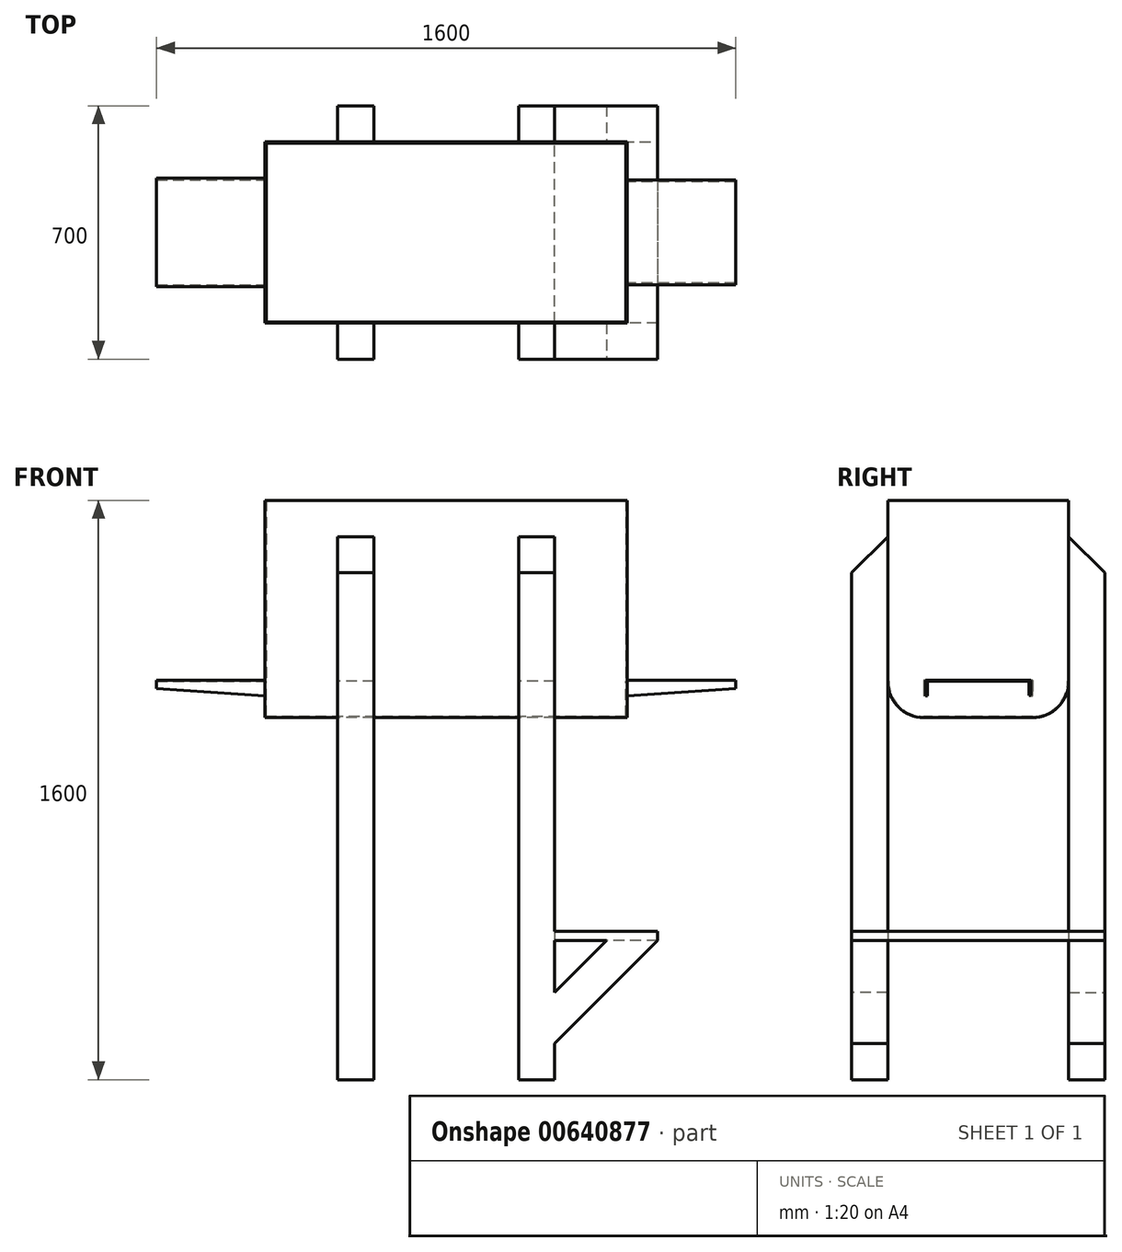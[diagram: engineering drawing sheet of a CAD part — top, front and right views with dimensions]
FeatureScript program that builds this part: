
annotation { "Feature Type Name" : "Feature", "Feature Type Description" : "" }
export const myFeature = defineFeature(function(context is Context, id is Id, definition is map)
    precondition{}
    {
        {
            var Q0;
            Q0=qCreatedBy(makeId("Right.planeOp"),FACE);
            var sketch = newSketch(context, id + "F0", { "sketchPlane" : qUnion([Q0])});
            skLineSegment(sketch, "E0", {"start": v(0, 632.77) * mm, "end": v(0, -64.43) * mm, "construction": true});
            skLineSegment(sketch, "E1", {"start": v(250, 600) * mm, "end": v(250, 100) * mm});
            skLineSegment(sketch, "E2", {"start": v(150, 0) * mm, "end": v(-150, 0) * mm});
            skLineSegment(sketch, "E3", {"start": v(-250, 100) * mm, "end": v(-250, 600) * mm});
            skPoint(sketch, "E4.visualSharp", {"position": v(250, 0) * mm});
            skArc(sketch, "E4.filletArc", {"start": v(150, 0) * mm, "mid": v(220.71, 29.29) * mm, "end": v(250, 100) * mm});
            skPoint(sketch, "E5.visualSharp", {"position": v(-250, 0) * mm});
            skArc(sketch, "E5.filletArc", {"start": v(-250, 100) * mm, "mid": v(-220.71, 29.29) * mm, "end": v(-150, 0) * mm});
            skLineSegment(sketch, "E6", {"start": v(250, 600) * mm, "end": v(-250, 600) * mm});
            skSolve(sketch);
        }
        {
            var Q0;
            Q0 = qSketchRegion(id + "F0", true);
            extrude(context, id + "F1", {"entities" : qUnion([Q0]), "depth" : 1000 * mm, "offsetDistance" : 25.4 * mm});
        }
        {
            var Q0;
            Q0=makeQuery(id+"F1.opExtrude","SWEPT_FACE",FACE,{"disambiguationData":[OSD([sQuery(id+"F0.wireOp",EDGE,"E6")])]});
            shell(context, id + "F2", {"entities" : qUnion([Q0]), "thickness" : 3 * mm});
        }
        {
            var Q0;
            Q0=makeQuery(id+"F1.opExtrude","CAP_FACE",FACE,{"disambiguationData":[OSD([sQuery(id+"F0.wireOp",EDGE,"E1"),sQuery(id+"F0.wireOp",EDGE,"E2"),sQuery(id+"F0.wireOp",EDGE,"E3"),sQuery(id+"F0.wireOp",EDGE,"E4.filletArc"),sQuery(id+"F0.wireOp",EDGE,"E5.filletArc"),sQuery(id+"F0.wireOp",EDGE,"E6")])],"isStart":true});
            var sketch = newSketch(context, id + "F3", { "sketchPlane" : qUnion([Q0])});
            skLineSegment(sketch, "E7.bottom", {"start": v(-150, 103) * mm, "end": v(150, 103) * mm});
            skLineSegment(sketch, "E7.top", {"start": v(-150, 100) * mm, "end": v(150, 100) * mm});
            skLineSegment(sketch, "E7.left", {"start": v(-150, 103) * mm, "end": v(-150, 100) * mm});
            skLineSegment(sketch, "E7.right", {"start": v(150, 103) * mm, "end": v(150, 100) * mm});
            skLineSegment(sketch, "E8", {"start": v(0, 372.57) * mm, "end": v(0, -47.43) * mm, "construction": true});
            skSolve(sketch);
        }
        {
            var Q0;
            Q0 = qSketchRegion(id + "F3", true);
            extrude(context, id + "F4", {"entities" : qUnion([Q0]), "operationType" : NewBodyOperationType.ADD, "depth" : 300 * mm, "offsetDistance" : 25.4 * mm});
        }
        {
            var Q0;
            Q0=makeQuery(id+"F4.opExtrude","SWEPT_FACE",FACE,{"disambiguationData":[OSD([sQuery(id+"F3.wireOp",EDGE,"E7.right")])]});
            var sketch = newSketch(context, id + "F5", { "sketchPlane" : qUnion([Q0])});
            skLineSegment(sketch, "E9", {"start": v(-300, 100) * mm, "end": v(-300, 80) * mm});
            skLineSegment(sketch, "E10", {"start": v(-300, 80) * mm, "end": v(0, 60) * mm});
            skLineSegment(sketch, "E11", {"start": v(0, 60) * mm, "end": v(0, 100) * mm});
            skLineSegment(sketch, "E12", {"start": v(-300, 100) * mm, "end": v(0, 100) * mm});
            skSolve(sketch);
        }
        {
            var Q0;
            Q0 = qSketchRegion(id + "F5", true);
            extrude(context, id + "F6", {"entities" : qUnion([Q0]), "operationType" : NewBodyOperationType.ADD, "oppositeDirection" : true, "depth" : 5 * mm, "offsetDistance" : 25.4 * mm});
        }
        {
            var Q0;
            Q0=makeQuery(id+"F4.opExtrude","SWEPT_FACE",FACE,{"disambiguationData":[OSD([sQuery(id+"F3.wireOp",EDGE,"E7.left")])]});
            var sketch = newSketch(context, id + "F7", { "sketchPlane" : qUnion([Q0])});
            skLineSegment(sketch, "E13", {"start": v(0, 100) * mm, "end": v(0, 60) * mm});
            skLineSegment(sketch, "E14", {"start": v(0, 60) * mm, "end": v(300, 80) * mm});
            skLineSegment(sketch, "E15", {"start": v(300, 80) * mm, "end": v(300, 100) * mm});
            skLineSegment(sketch, "E16", {"start": v(300, 100) * mm, "end": v(0, 100) * mm});
            skSolve(sketch);
        }
        {
            var Q0;
            Q0 = qSketchRegion(id + "F7", true);
            extrude(context, id + "F8", {"entities" : qUnion([Q0]), "operationType" : NewBodyOperationType.ADD, "oppositeDirection" : true, "depth" : 5 * mm, "offsetDistance" : 25.4 * mm});
        }
        {
            var Q0;
            Q0=makeQuery(id+"F1.opExtrude","SWEPT_FACE",FACE,{"disambiguationData":[OSD([sQuery(id+"F0.wireOp",EDGE,"E3")])]});
            var sketch = newSketch(context, id + "F9", { "sketchPlane" : qUnion([Q0])});
            skLineSegment(sketch, "E17", {"start": v(500, 727.75) * mm, "end": v(500, -77.26) * mm, "construction": true});
            skPoint(sketch, "E17.startSnap0", {"position": v(500, 600) * mm});
            skLineSegment(sketch, "E18.bottom", {"start": v(200, 500) * mm, "end": v(300, 500) * mm});
            skLineSegment(sketch, "E18.top", {"start": v(200, -1000) * mm, "end": v(300, -1000) * mm});
            skLineSegment(sketch, "E18.left", {"start": v(200, 500) * mm, "end": v(200, -1000) * mm});
            skLineSegment(sketch, "E18.right", {"start": v(300, 500) * mm, "end": v(300, -1000) * mm});
            skLineSegment(sketch, "E19.bottom", {"start": v(700, 500) * mm, "end": v(800, 500) * mm});
            skLineSegment(sketch, "E19.top", {"start": v(700, -1000) * mm, "end": v(800, -1000) * mm});
            skLineSegment(sketch, "E19.left", {"start": v(700, 500) * mm, "end": v(700, -1000) * mm});
            skLineSegment(sketch, "E19.right", {"start": v(800, 500) * mm, "end": v(800, -1000) * mm});
            skSolve(sketch);
        }
        {
            var Q0;
            Q0 = qSketchRegion(id + "F9", true);
            extrude(context, id + "F10", {"entities" : qUnion([Q0]), "operationType" : NewBodyOperationType.ADD, "depth" : 100 * mm, "offsetDistance" : 25.4 * mm});
        }
        {
            var Q0;
            Q0=makeQuery(id+"F10.opExtrude","SWEPT_FACE",FACE,{"disambiguationData":[OSD([sQuery(id+"F9.wireOp",EDGE,"E18.left")])]});
            var sketch = newSketch(context, id + "F11", { "sketchPlane" : qUnion([Q0])});
            skLineSegment(sketch, "E20", {"start": v(250, 500) * mm, "end": v(350, 400) * mm});
            skLineSegment(sketch, "E21", {"start": v(350, 400) * mm, "end": v(350, 500) * mm});
            skLineSegment(sketch, "E22", {"start": v(350, 500) * mm, "end": v(250, 500) * mm});
            skSolve(sketch);
        }
        {
            var Q0;
            Q0 = qSketchRegion(id + "F11", true);
            extrude(context, id + "F12", {"entities" : qUnion([Q0]), "operationType" : NewBodyOperationType.REMOVE, "endBound" : BoundingType.THROUGH_ALL, "oppositeDirection" : true, "depth" : 25.4 * mm, "offsetDistance" : 25.4 * mm});
        }
        {
            var Q0;
            Q0=makeQuery(id+"F1.opExtrude","SWEPT_FACE",FACE,{"disambiguationData":[OSD([sQuery(id+"F0.wireOp",EDGE,"E1")])]});
            var sketch = newSketch(context, id + "F13", { "sketchPlane" : qUnion([Q0])});
            skLineSegment(sketch, "E23", {"start": v(-500, 832.8) * mm, "end": v(-500, -264.24) * mm, "construction": true});
            skPoint(sketch, "E23.startSnap0", {"position": v(-500, 100) * mm});
            skLineSegment(sketch, "E24.bottom", {"start": v(-800, 500) * mm, "end": v(-700, 500) * mm});
            skLineSegment(sketch, "E24.top", {"start": v(-800, -1000) * mm, "end": v(-700, -1000) * mm});
            skLineSegment(sketch, "E24.left", {"start": v(-800, 500) * mm, "end": v(-800, -1000) * mm});
            skLineSegment(sketch, "E24.right", {"start": v(-700, 500) * mm, "end": v(-700, -1000) * mm});
            skLineSegment(sketch, "E25.bottom", {"start": v(-300, 500) * mm, "end": v(-200, 500) * mm});
            skLineSegment(sketch, "E25.top", {"start": v(-300, -1000) * mm, "end": v(-200, -1000) * mm});
            skLineSegment(sketch, "E25.left", {"start": v(-300, 500) * mm, "end": v(-300, -1000) * mm});
            skLineSegment(sketch, "E25.right", {"start": v(-200, 500) * mm, "end": v(-200, -1000) * mm});
            skSolve(sketch);
        }
        {
            var Q0;
            Q0 = qSketchRegion(id + "F13", true);
            extrude(context, id + "F14", {"entities" : qUnion([Q0]), "operationType" : NewBodyOperationType.ADD, "depth" : 100 * mm, "offsetDistance" : 25.4 * mm});
        }
        {
            var Q0;
            Q0=makeQuery(id+"F14.opExtrude","SWEPT_FACE",FACE,{"disambiguationData":[OSD([sQuery(id+"F13.wireOp",EDGE,"E24.left")])]});
            var sketch = newSketch(context, id + "F15", { "sketchPlane" : qUnion([Q0])});
            skLineSegment(sketch, "E26", {"start": v(250, 500) * mm, "end": v(350, 400) * mm});
            skLineSegment(sketch, "E27", {"start": v(350, 400) * mm, "end": v(350, 500) * mm});
            skLineSegment(sketch, "E28", {"start": v(350, 500) * mm, "end": v(250, 500) * mm});
            skSolve(sketch);
        }
        {
            var Q0;
            Q0 = qSketchRegion(id + "F15", true);
            extrude(context, id + "F16", {"entities" : qUnion([Q0]), "operationType" : NewBodyOperationType.REMOVE, "endBound" : BoundingType.THROUGH_ALL, "oppositeDirection" : true, "depth" : 25.4 * mm, "offsetDistance" : 25.4 * mm});
        }
        {
            var Q0;
            Q0=makeQuery(id+"F1.opExtrude","CAP_FACE",FACE,{"disambiguationData":[OSD([sQuery(id+"F0.wireOp",EDGE,"E1"),sQuery(id+"F0.wireOp",EDGE,"E2"),sQuery(id+"F0.wireOp",EDGE,"E3"),sQuery(id+"F0.wireOp",EDGE,"E4.filletArc"),sQuery(id+"F0.wireOp",EDGE,"E5.filletArc"),sQuery(id+"F0.wireOp",EDGE,"E6")])],"isStart":false});
            var sketch = newSketch(context, id + "F17", { "sketchPlane" : qUnion([Q0])});
            skLineSegment(sketch, "E29.bottom", {"start": v(-145, 103) * mm, "end": v(145, 103) * mm});
            skLineSegment(sketch, "E29.top", {"start": v(-145, 100) * mm, "end": v(145, 100) * mm});
            skLineSegment(sketch, "E29.left", {"start": v(-145, 103) * mm, "end": v(-145, 100) * mm});
            skLineSegment(sketch, "E29.right", {"start": v(145, 103) * mm, "end": v(145, 100) * mm});
            skLineSegment(sketch, "E30", {"start": v(0, 538.1) * mm, "end": v(0, -341.27) * mm, "construction": true});
            skSolve(sketch);
        }
        {
            var Q0;
            Q0 = qSketchRegion(id + "F17", true);
            extrude(context, id + "F18", {"entities" : qUnion([Q0]), "operationType" : NewBodyOperationType.ADD, "depth" : 300 * mm, "offsetDistance" : 25.4 * mm});
        }
        {
            var Q0;
            Q0=makeQuery(id+"F18.opExtrude","SWEPT_FACE",FACE,{"disambiguationData":[OSD([sQuery(id+"F17.wireOp",EDGE,"E29.left")])]});
            var sketch = newSketch(context, id + "F19", { "sketchPlane" : qUnion([Q0])});
            skLineSegment(sketch, "E31", {"start": v(1000, 100) * mm, "end": v(1000, 60) * mm});
            skLineSegment(sketch, "E32", {"start": v(1000, 60) * mm, "end": v(1300, 80) * mm});
            skLineSegment(sketch, "E33", {"start": v(1300, 80) * mm, "end": v(1300, 100) * mm});
            skLineSegment(sketch, "E34", {"start": v(1300, 100) * mm, "end": v(1000, 100) * mm});
            skSolve(sketch);
        }
        {
            var Q0;
            Q0 = qSketchRegion(id + "F19", true);
            extrude(context, id + "F20", {"entities" : qUnion([Q0]), "operationType" : NewBodyOperationType.ADD, "oppositeDirection" : true, "depth" : 5 * mm, "offsetDistance" : 25.4 * mm});
        }
        {
            var Q0;
            Q0=makeQuery(id+"F18.opExtrude","SWEPT_FACE",FACE,{"disambiguationData":[OSD([sQuery(id+"F17.wireOp",EDGE,"E29.right")])]});
            var sketch = newSketch(context, id + "F21", { "sketchPlane" : qUnion([Q0])});
            skLineSegment(sketch, "E35", {"start": v(-1300, 100) * mm, "end": v(-1300, 80) * mm});
            skLineSegment(sketch, "E36", {"start": v(-1300, 80) * mm, "end": v(-1000, 60.64) * mm});
            skLineSegment(sketch, "E37", {"start": v(-1000, 60.64) * mm, "end": v(-1000, 100) * mm});
            skLineSegment(sketch, "E38", {"start": v(-1000, 100) * mm, "end": v(-1300, 100) * mm});
            skSolve(sketch);
        }
        {
            var Q0;
            Q0 = qSketchRegion(id + "F21", true);
            extrude(context, id + "F22", {"entities" : qUnion([Q0]), "operationType" : NewBodyOperationType.ADD, "oppositeDirection" : true, "depth" : 5 * mm, "offsetDistance" : 25.4 * mm});
        }
        {
            var Q0;
            Q0=makeQuery(id+"F10.opExtrude","CAP_FACE",FACE,{"disambiguationData":[OSD([sQuery(id+"F9.wireOp",EDGE,"E19.bottom"),sQuery(id+"F9.wireOp",EDGE,"E19.top"),sQuery(id+"F9.wireOp",EDGE,"E19.left"),sQuery(id+"F9.wireOp",EDGE,"E19.right")])],"isStart":false});
            var sketch = newSketch(context, id + "F23", { "sketchPlane" : qUnion([Q0])});
            skLineSegment(sketch, "E39", {"start": v(800, -900) * mm, "end": v(1084.35, -615.65) * mm});
            skLineSegment(sketch, "E40", {"start": v(1084.35, -615.65) * mm, "end": v(1013.64, -544.94) * mm});
            skLineSegment(sketch, "E41", {"start": v(1013.64, -544.94) * mm, "end": v(800, -758.58) * mm});
            skLineSegment(sketch, "E42", {"start": v(800, -758.58) * mm, "end": v(800, -900) * mm});
            skSolve(sketch);
        }
        {
            var Q0;
            Q0 = qSketchRegion(id + "F23", true);
            var Q1;
            Q1=makeQuery(id+"F10.opExtrude","CAP_FACE",FACE,{"disambiguationData":[OSD([sQuery(id+"F9.wireOp",EDGE,"E19.bottom"),sQuery(id+"F9.wireOp",EDGE,"E19.top"),sQuery(id+"F9.wireOp",EDGE,"E19.left"),sQuery(id+"F9.wireOp",EDGE,"E19.right")])],"isStart":true});
            extrude(context, id + "F24", {"entities" : qUnion([Q0]), "operationType" : NewBodyOperationType.ADD, "endBound" : BoundingType.UP_TO_SURFACE, "oppositeDirection" : true, "depth" : 25.4 * mm, "endBoundEntityFace" : qUnion([Q1]), "offsetDistance" : 25.4 * mm});
        }
        {
            var Q0;
            Q0=makeQuery(id+"F14.opExtrude","CAP_FACE",FACE,{"disambiguationData":[OSD([sQuery(id+"F13.wireOp",EDGE,"E24.bottom"),sQuery(id+"F13.wireOp",EDGE,"E24.top"),sQuery(id+"F13.wireOp",EDGE,"E24.left"),sQuery(id+"F13.wireOp",EDGE,"E24.right")])],"isStart":false});
            var sketch = newSketch(context, id + "F25", { "sketchPlane" : qUnion([Q0])});
            skLineSegment(sketch, "E43", {"start": v(-800, -900) * mm, "end": v(-800, -758.58) * mm});
            skLineSegment(sketch, "E44", {"start": v(-800, -758.58) * mm, "end": v(-1013.64, -544.94) * mm});
            skLineSegment(sketch, "E45", {"start": v(-1013.64, -544.94) * mm, "end": v(-1084.35, -615.65) * mm});
            skLineSegment(sketch, "E46", {"start": v(-1084.35, -615.65) * mm, "end": v(-800, -900) * mm});
            skSolve(sketch);
        }
        {
            var Q0;
            Q0 = qSketchRegion(id + "F25", true);
            extrude(context, id + "F26", {"entities" : qUnion([Q0]), "operationType" : NewBodyOperationType.ADD, "oppositeDirection" : true, "depth" : 100 * mm, "offsetDistance" : 25.4 * mm});
        }
        {
            var Q0;
            Q0=makeQuery(id+"F24.boolean.opBoolean","MERGE",FACE,{"derivedFrom":[makeQuery(id+"F10.opExtrude","CAP_FACE",FACE,{"disambiguationData":[OSD([sQuery(id+"F9.wireOp",EDGE,"E19.bottom"),sQuery(id+"F9.wireOp",EDGE,"E19.top"),sQuery(id+"F9.wireOp",EDGE,"E19.left"),sQuery(id+"F9.wireOp",EDGE,"E19.right")])],"isStart":false}),makeQuery(id+"F24.opExtrude","CAP_FACE",FACE,{"disambiguationData":[OSD([sQuery(id+"F23.wireOp",EDGE,"E39"),sQuery(id+"F23.wireOp",EDGE,"E40"),sQuery(id+"F23.wireOp",EDGE,"E41"),sQuery(id+"F23.wireOp",EDGE,"E42")])],"isStart":true})]});
            var sketch = newSketch(context, id + "F27", { "sketchPlane" : qUnion([Q0])});
            skLineSegment(sketch, "E47", {"start": v(1084.35, -615.65) * mm, "end": v(942.92, -615.65) * mm});
            skLineSegment(sketch, "E48", {"start": v(942.92, -615.65) * mm, "end": v(1013.64, -544.94) * mm});
            skLineSegment(sketch, "E49", {"start": v(1013.64, -544.94) * mm, "end": v(1084.35, -615.65) * mm});
            skSolve(sketch);
        }
        {
            var Q0;
            Q0 = qSketchRegion(id + "F27", true);
            extrude(context, id + "F28", {"entities" : qUnion([Q0]), "operationType" : NewBodyOperationType.REMOVE, "oppositeDirection" : true, "depth" : 744.22 * mm, "offsetDistance" : 25.4 * mm});
        }
        {
            var Q0;
            {var subQ3=sQuery(id+"F23.wireOp",EDGE,"E39");Q0=makeQuery(id+"F28.boolean.opBoolean","COPY",FACE,{"disambiguationData":[TD([makeQuery(id+"F24.opExtrude","SWEPT_FACE",FACE,{"disambiguationData":[OSD([subQ3])]})])],"derivedFrom":makeQuery(id+"F28.opExtrude","SWEPT_FACE",FACE,{"disambiguationData":[OSD([sQuery(id+"F27.wireOp",EDGE,"E47")])]})});}
            var sketch = newSketch(context, id + "F29", { "sketchPlane" : qUnion([Q0])});
            skLineSegment(sketch, "E50.bottom", {"start": v(1084.35, -350) * mm, "end": v(800, -350) * mm});
            skLineSegment(sketch, "E50.top", {"start": v(1084.35, 350) * mm, "end": v(800, 350) * mm});
            skLineSegment(sketch, "E50.left", {"start": v(1084.35, -350) * mm, "end": v(1084.35, 350) * mm});
            skLineSegment(sketch, "E50.right", {"start": v(800, -350) * mm, "end": v(800, 350) * mm});
            skSolve(sketch);
        }
        {
            var Q0;
            Q0 = qSketchRegion(id + "F29", true);
            extrude(context, id + "F30", {"entities" : qUnion([Q0]), "operationType" : NewBodyOperationType.ADD, "depth" : 25.4 * mm, "offsetDistance" : 25.4 * mm});
        }
    });
